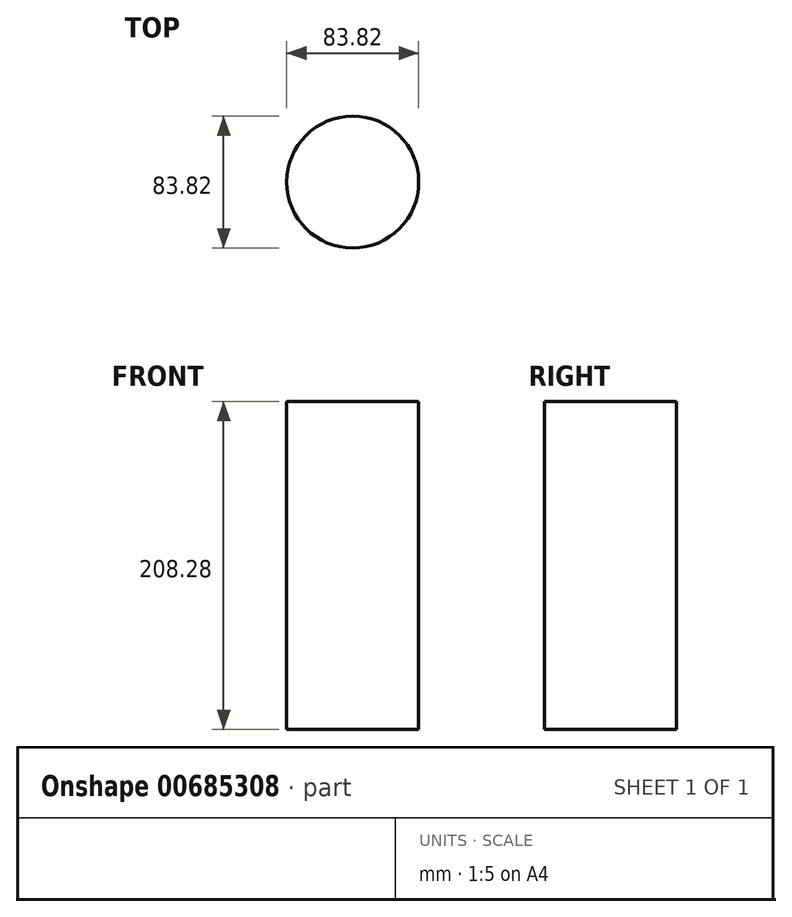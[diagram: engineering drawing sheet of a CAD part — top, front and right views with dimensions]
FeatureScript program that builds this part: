
annotation { "Feature Type Name" : "Feature", "Feature Type Description" : "" }
export const myFeature = defineFeature(function(context is Context, id is Id, definition is map)
    precondition{}
    {
        {
            var Q0;
            Q0=qCreatedBy(makeId("Top.planeOp"),FACE);
            var sketch = newSketch(context, id + "F0", { "sketchPlane" : qUnion([Q0])});
            skCircle(sketch, "E0", {"center": v(0, 0) * mm, "radius": 41.91 * mm});
            skSolve(sketch);
        }
        {
            var Q0;
            Q0 = qSketchRegion(id + "F0", true);
            extrude(context, id + "F1", {"entities" : qUnion([Q0]), "depth" : 208.28 * mm, "offsetDistance" : 25.4 * mm});
        }
    });
